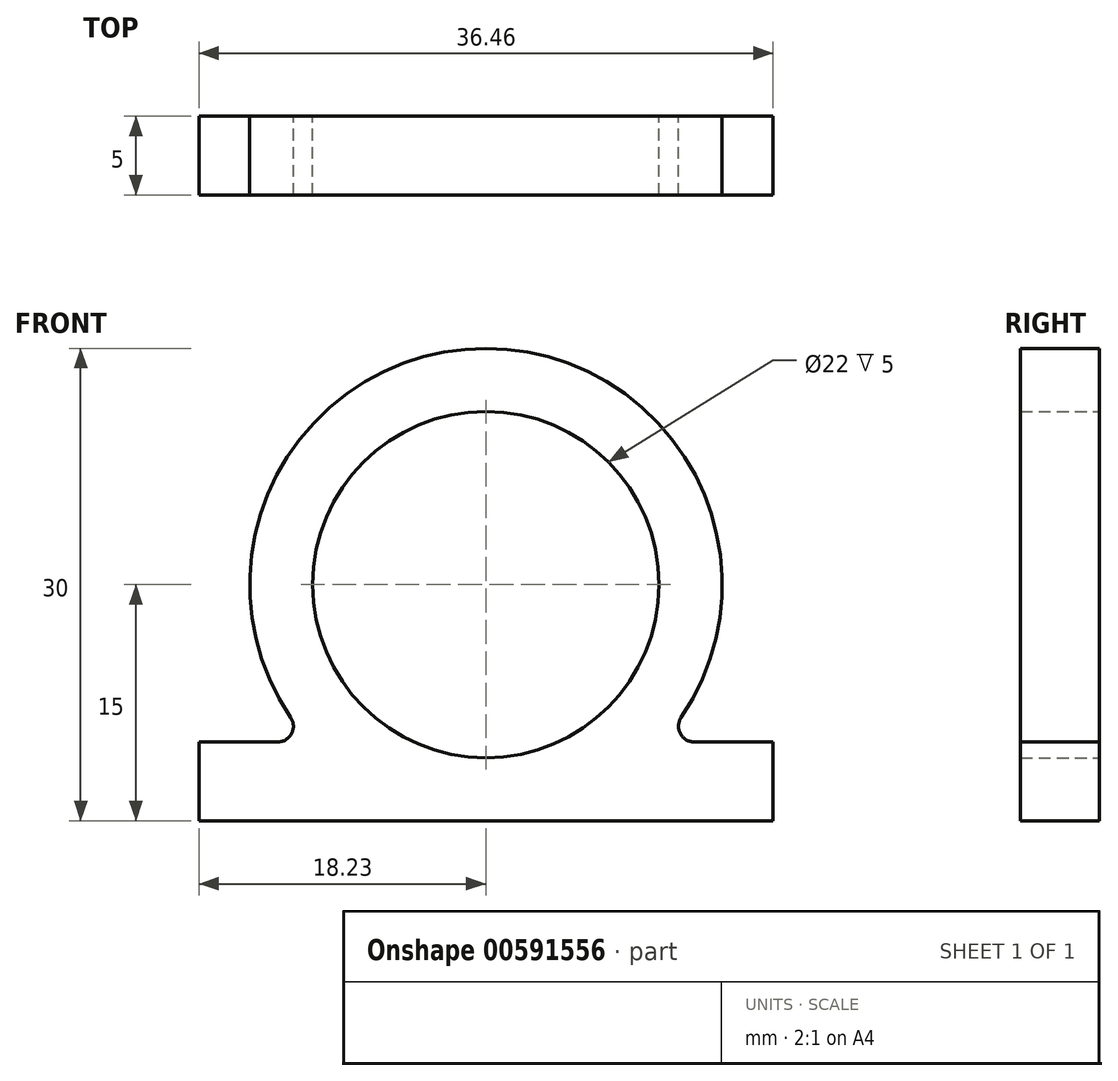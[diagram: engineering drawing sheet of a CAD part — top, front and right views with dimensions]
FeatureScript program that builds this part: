
annotation { "Feature Type Name" : "Feature", "Feature Type Description" : "" }
export const myFeature = defineFeature(function(context is Context, id is Id, definition is map)
    precondition{}
    {
        {
            var Q0;
            Q0=qCreatedBy(makeId("Front.planeOp"),FACE);
            var sketch = newSketch(context, id + "F0", { "sketchPlane" : qUnion([Q0])});
            skCircle(sketch, "E0", {"center": v(0, 0) * mm, "radius": 11 * mm});
            skArc(sketch, "E1", {"start": v(12.4, -8.44) * mm, "mid": v(0, 15) * mm, "end": v(-12.4, -8.44) * mm});
            skLineSegment(sketch, "E2.bottom", {"start": v(-18.23, -15) * mm, "end": v(18.23, -15) * mm});
            skLineSegment(sketch, "E2.top", {"start": v(-18.23, -10) * mm, "end": v(-13.23, -10) * mm});
            skLineSegment(sketch, "E2.left", {"start": v(-18.23, -15) * mm, "end": v(-18.23, -10) * mm});
            skLineSegment(sketch, "E2.right", {"start": v(18.23, -15) * mm, "end": v(18.23, -10) * mm});
            skPoint(sketch, "E3", {"position": v(0, -15) * mm});
            skLineSegment(sketch, "E4.trimOffspring", {"start": v(13.23, -10) * mm, "end": v(18.23, -10) * mm});
            skPoint(sketch, "E5.visualSharp", {"position": v(-11.18, -10) * mm});
            skArc(sketch, "E5.filletArc", {"start": v(-13.23, -10) * mm, "mid": v(-12.34, -9.47) * mm, "end": v(-12.4, -8.44) * mm});
            skPoint(sketch, "E6.visualSharp", {"position": v(11.18, -10) * mm});
            skArc(sketch, "E6.filletArc", {"start": v(12.4, -8.44) * mm, "mid": v(12.34, -9.47) * mm, "end": v(13.23, -10) * mm});
            skSolve(sketch);
        }
        {
            var Q0;
            Q0 = qSketchRegion(id + "F0", true);
            extrude(context, id + "F1", {"entities" : qUnion([Q0]), "depth" : 5 * mm, "offsetDistance" : 25 * mm});
        }
    });
